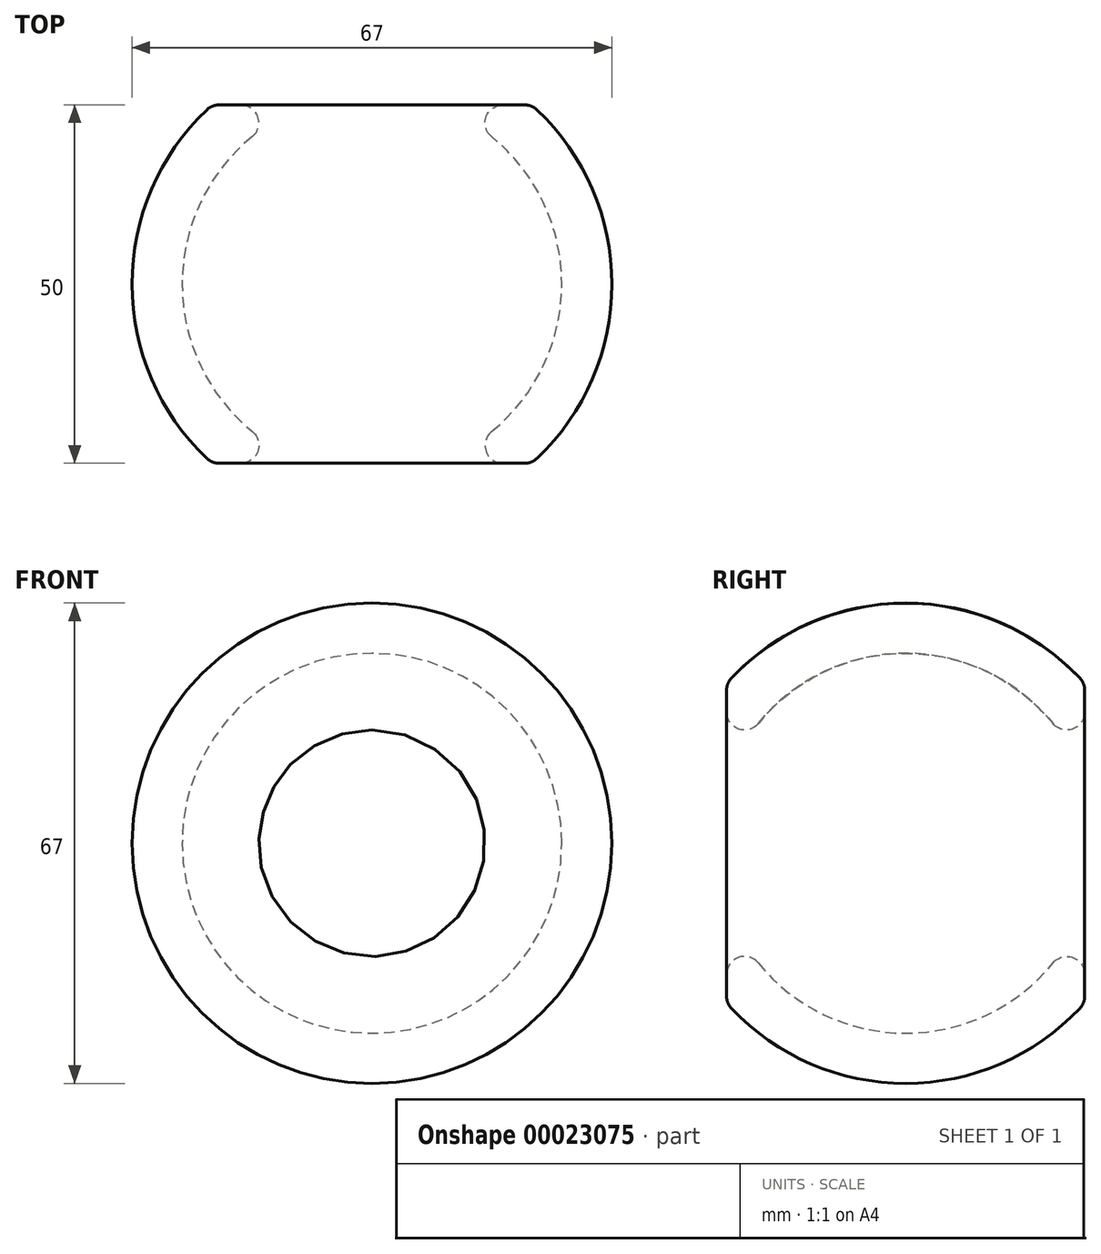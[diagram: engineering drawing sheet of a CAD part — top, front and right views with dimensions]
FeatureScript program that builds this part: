
annotation { "Feature Type Name" : "Feature", "Feature Type Description" : "" }
export const myFeature = defineFeature(function(context is Context, id is Id, definition is map)
    precondition{}
    {
        {
            var Q0;
            Q0=qCreatedBy(makeId("Top.planeOp"),FACE);
            var sketch = newSketch(context, id + "F0", { "sketchPlane" : qUnion([Q0])});
            skArc(sketch, "E0", {"start": v(-23.04, 24.31) * mm, "mid": v(-33.5, 0) * mm, "end": v(-23.04, -24.31) * mm});
            skLineSegment(sketch, "E1", {"start": v(-21.32, 25) * mm, "end": v(-18.3, 25) * mm});
            skLineSegment(sketch, "E2", {"start": v(-18.3, -25) * mm, "end": v(-21.32, -25) * mm});
            skArc(sketch, "E3", {"start": v(-16.72, 20.56) * mm, "mid": v(-26.5, 0) * mm, "end": v(-16.72, -20.56) * mm});
            skPoint(sketch, "E4", {"position": v(-26.5, 0) * mm});
            skPoint(sketch, "E5", {"position": v(-33.5, 0) * mm});
            skPoint(sketch, "E6.visualSharp", {"position": v(-22.3, 25) * mm});
            skArc(sketch, "E6.filletArc", {"start": v(-21.32, 25) * mm, "mid": v(-22.25, 24.82) * mm, "end": v(-23.04, 24.31) * mm});
            skPoint(sketch, "E7.visualSharp", {"position": v(-8.79, 25) * mm});
            skArc(sketch, "E7.filletArc", {"start": v(-16.72, 20.56) * mm, "mid": v(-15.94, 23.34) * mm, "end": v(-18.3, 25) * mm});
            skPoint(sketch, "E8.visualSharp", {"position": v(-22.3, -25) * mm});
            skArc(sketch, "E8.filletArc", {"start": v(-23.04, -24.31) * mm, "mid": v(-22.25, -24.82) * mm, "end": v(-21.32, -25) * mm});
            skPoint(sketch, "E9.visualSharp", {"position": v(-8.79, -25) * mm});
            skArc(sketch, "E9.filletArc", {"start": v(-18.3, -25) * mm, "mid": v(-15.94, -23.34) * mm, "end": v(-16.72, -20.56) * mm});
            skLineSegment(sketch, "E10", {"start": v(0, 22.58) * mm, "end": v(0, -20.14) * mm, "construction": true});
            skSolve(sketch);
        }
        {
            var Q0;
            Q0 = qSketchRegion(id + "F0", true);
            var Q1;
            Q1=sQuery(id+"F0.wireOp",EDGE,"E10");
            revolve(context, id + "F1", {"entities" : qUnion([Q0]), "axis" : qUnion([Q1]), "revolveType" : RevolveType.FULL});
        }
    });
